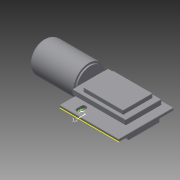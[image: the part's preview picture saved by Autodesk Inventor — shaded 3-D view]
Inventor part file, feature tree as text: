
AUTODESK INVENTOR PART (.ipt)
format: ipt  version: 2015 (Build 190159000, 159)  size: 230,912 bytes
history: native  units: in
note: dims shown in document units (in); Inventor stores cm internally (conversion verified against a paired STEP export)
features: extrude x7, sketch x7, fillet x2
ambient origin geometry x8: Origin, YZ Plane, XZ Plane, XY Plane, X Axis, Y Axis, Z Axis, Center Point
bodies: Solid1 (feature_tree)
feature tree (16):
  extrude  "Extrusion1"  Depth=0.9843in
  extrude  "Extrusion2"  Depth=0.6535in
  extrude  "Extrusion3"  Depth=0.1102in
  extrude  "Extrusion4"  Depth=0.1417in TaperAngle=0.0deg
  extrude  "Extrusion5"  Depth=0.0945in
  fillet  "Fillet1"  Radius=0.0512in
  extrude  "Extrusion6"  Depth=0.0787in TaperAngle=0.0deg
  extrude  "Extrusion7"  Depth=0.0079in TaperAngle=0.0deg
  fillet  "Fillet2"  Radius=0.5118in
  sketch  "Sketch1"  dims[d0=0.9055in d1=0.9843in]
  sketch  "Sketch2"  dims[d2=0.0394in d3=0.0in d4=0.6535in]
  sketch  "Sketch3"  dims[d5=0.4882in d6=0.1102in]
  sketch  "Sketch4"  dims[d7=0.2362in d8=0.1417in d9=0.0in]
  sketch  "Sketch6"  dims[d11=0.0512in d12=0.0945in d13=0.0512in]
  sketch  "Sketch7"  dims[d14=0.1339in d15=0.0787in d16=0.0in]
  sketch  "Sketch8"  dims[d17=0.4488in d18=0.7874in d19=0.0in d20=0.5118in d21=0.7638in d22=0.0in d23=0.0984in d24=0.6299in d25=0.5118in d26=0.0512in d27=0.1811in d28=0.1102in d29=0.0in d37=0.1102in d38=0.0in d39=0.0079in]
